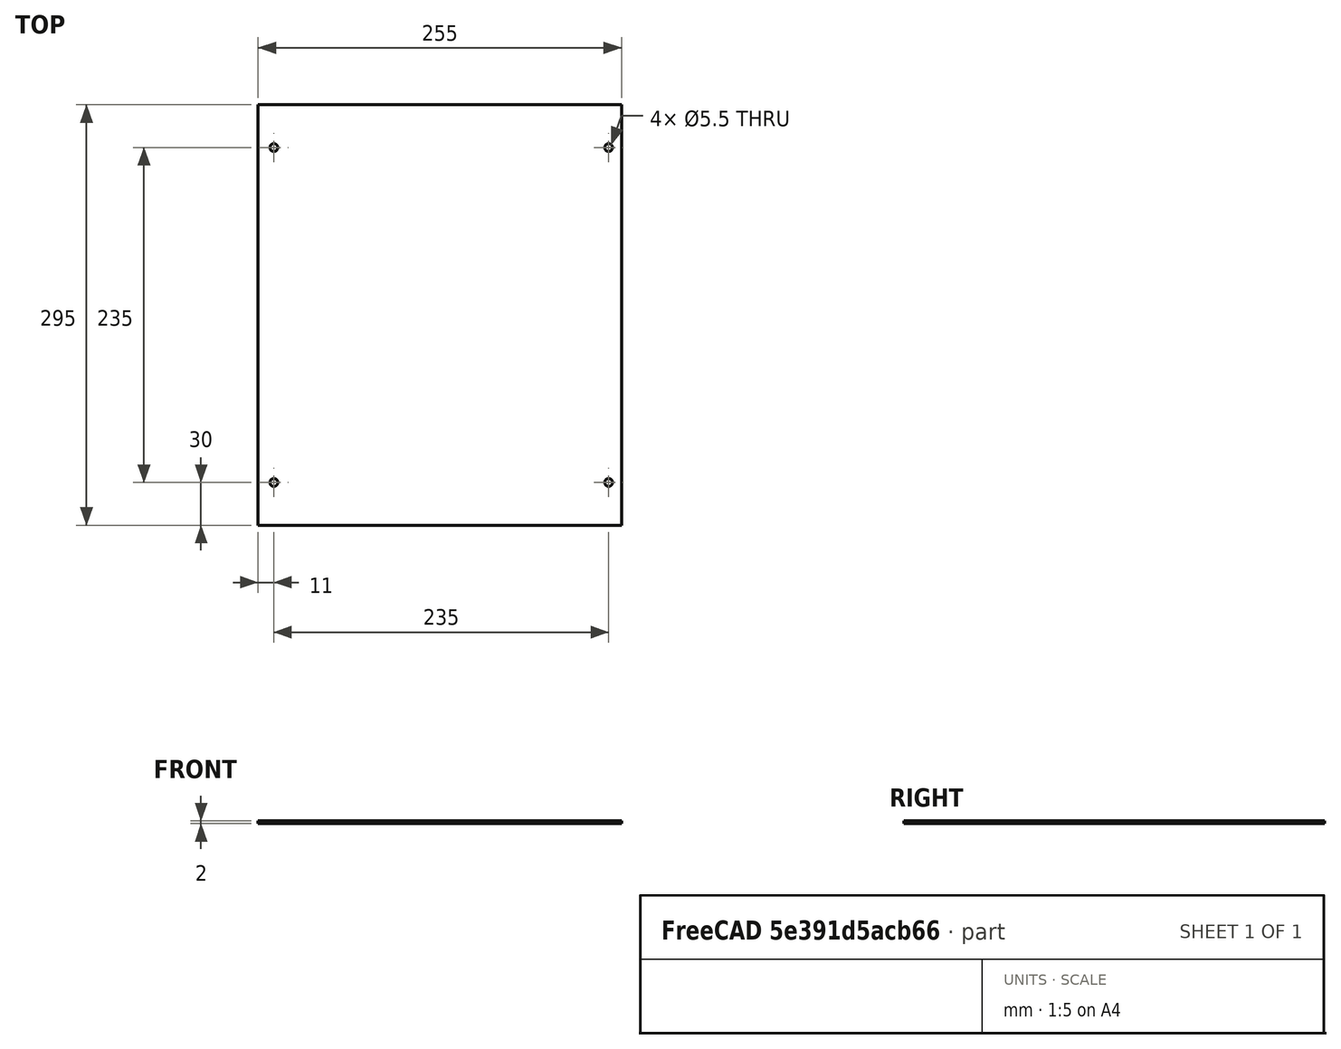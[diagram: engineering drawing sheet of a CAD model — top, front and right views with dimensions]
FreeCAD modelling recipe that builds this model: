
FCSTD DOCUMENT  (FreeCAD 0.15R4671 (Git))
Label: bottom2
License: All rights reserved
LicenseURL: http://en.wikipedia.org/wiki/All_rights_reserved
objects: Drawing::FeatureViewPython×5, Part::Cylinder×4, Part::Cut×4, Part::Box×1, Drawing::FeatureViewPart×1, Drawing::FeaturePage×1
note: 9 computed .brp shape members not serialized (recipe doc carries the construction recipe); baked Part::Feature solids carry a one-line shape summary decoded from their .brp

FEATURE [Part::Box] Box  label="Cube"
  Height = 2
  Length = 255
  Placement = pos=(-1,0,1.5332e-08) rot=(0,0,1;0rad)
  Width = 295
FEATURE [Part::Cylinder] Cylinder
  Angle = 360
  Height = 10
  Placement = pos=(10,30,-5) rot=(0,0,1;0rad)
  Radius = 2.75
FEATURE [Part::Cylinder] Cylinder001
  Angle = 360
  Height = 10
  Placement = pos=(10,265,-5) rot=(0,0,1;0rad)
  Radius = 2.75
FEATURE [Part::Cylinder] Cylinder002
  Angle = 360
  Height = 10
  Placement = pos=(245,30,-5) rot=(0,0,1;0rad)
  Radius = 2.75
FEATURE [Part::Cylinder] Cylinder003
  Angle = 360
  Height = 10
  Placement = pos=(245,265,-5) rot=(0,0,1;0rad)
  Radius = 2.75
FEATURE [Part::Cut] Cut
  Base = -> Box
  Tool = -> Cylinder
FEATURE [Part::Cut] Cut001
  Base = -> Cut
  Tool = -> Cylinder001
FEATURE [Part::Cut] Cut002
  Base = -> Cut001
  Tool = -> Cylinder002
FEATURE [Part::Cut] Cut003
  Base = -> Cut002
  Tool = -> Cylinder003
FEATURE [Drawing::FeatureViewPart] Ortho  label="Ortho_0_0"
  Direction = (0,0,1)
  HiddenWidth = 0.15
  LineWidth = 0.35
  Rotation = 0
  Scale = 0.5
  ShowHiddenLines = false
  ShowSmoothLines = false
  Source = -> Cut003
  Tolerance = 0.05
  ViewResult = <g id="Ortho_0_0"\n   transform="rotate(0,46.75,192.25) translate(46.75,192.25) scale(0.5,0.5)"\n  >\n<g   stroke="rgb(0, 0, 0)"\n   stroke-width="0.7"\n   stroke-linecap="butt"\n   stroke-linejoin="miter"\n   fill="none"\n   transform="scale(1,-1)"\n  >\n<path id= "1" d=" M -1 0 L -1 295 " />\n<path id= "2" d=" M -1 0 L 254 0 " />\n<path id= "3" d=" M -1 295 L 254 295 " />\n<path id= "4" d=" M 254 0 L 254 295 " />\n<circle cx ="245" cy ="265" r ="2.75" /><circle cx ="10" cy ="265" r ="2.75" /><circle cx ="245" cy ="30" r ="2.75" /><circle cx ="10" cy ="30" r ="2.75" /></g>\n</g>
  Visible = true
  X = 46.75
  Y = 192.25
FEATURE [Drawing::FeatureViewPython] dim001  # drawing view (typed FeaturePython)
  Rotation = 0
  ViewResult = <g> \n  <line x1="44.250000" y1="192.250000" x2="37.066293" y2="192.250000" style="stroke:rgb(0,0,255);stroke-width:0.50" />\n<line x1="44.250000" y1="44.750000" x2="37.066293" y2="44.750000" style="stroke:rgb(0,0,255);stroke-width:0.50" />\n<line x1="38.066293" y1="192.250000" x2="38.066293" y2="44.750000" style="stroke:rgb(0,0,255);stroke-width:0.50" /> \n  <polygon points="38.066293,44.750000 37.066293,47.750000 38.066293,48.750000 39.066293,47.750000" style="fill:rgb(0,0,255);stroke:rgb(0,0,255);stroke-width:0" /><polygon points="38.066293,192.250000 39.066293,189.250000 38.066293,188.250000 37.066293,189.250000" style="fill:rgb(0,0,255);stroke:rgb(0,0,255);stroke-width:0" /> \n  <text x="36.066293" y="118.500000" font-family="inherit" font-size="3.6" fill="rgb(0,0,255)" text-anchor="middle" transform="rotate(-90.000000 36.066293,118.500000)" >295</text> </g>
  Visible = true
  X = 0
  Y = 0
  arrowL1 = 3
  arrowL2 = 1
  arrowW = 2
  arrow_scheme = 0
  autoPlaceOffset = 2
  autoPlaceText = true
  click1_x = 38.0663
  click1_y = 84.7282
  click2_x = 38.0663
  click2_y = 84.7282
  comma_decimal_place = false
  dimension_line_overshoot = 1
  gap_datum_points = 2
  halfDimension_linear = false
  lineColor = rgb(0,0,255)
  strokeWidth = 0.5
  textFormat_linear = %(value)3.3f
  textRenderer_color = rgb(0,0,255)
  textRenderer_family = inherit
  textRenderer_size = 3.6
  unit_custom_scale = 1
  unit_scheme = 0
FEATURE [Drawing::FeatureViewPython] dim002  # drawing view (typed FeaturePython)
  Rotation = 0
  ViewResult = <g> \n  <line x1="46.250000" y1="42.750000" x2="46.250000" y2="32.154514" style="stroke:rgb(0,0,255);stroke-width:0.50" />\n<line x1="173.750000" y1="42.750000" x2="173.750000" y2="32.154514" style="stroke:rgb(0,0,255);stroke-width:0.50" />\n<line x1="46.250000" y1="33.154514" x2="173.750000" y2="33.154514" style="stroke:rgb(0,0,255);stroke-width:0.50" /> \n  <polygon points="173.750000,33.154514 170.750000,32.154514 169.750000,33.154514 170.750000,34.154514" style="fill:rgb(0,0,255);stroke:rgb(0,0,255);stroke-width:0" /><polygon points="46.250000,33.154514 49.250000,34.154514 50.250000,33.154514 49.250000,32.154514" style="fill:rgb(0,0,255);stroke:rgb(0,0,255);stroke-width:0" /> \n  <text x="110.000000" y="31.154514" font-family="inherit" font-size="3.6" fill="rgb(0,0,255)" text-anchor="middle" transform="rotate(0.000000 110.000000,31.154514)" >255</text> </g>
  Visible = true
  X = 0
  Y = 0
  arrowL1 = 3
  arrowL2 = 1
  arrowW = 2
  arrow_scheme = 0
  autoPlaceOffset = 2
  autoPlaceText = true
  click1_x = 111.334
  click1_y = 33.1545
  click2_x = 111.334
  click2_y = 33.1545
  comma_decimal_place = false
  dimension_line_overshoot = 1
  gap_datum_points = 2
  halfDimension_linear = false
  lineColor = rgb(0,0,255)
  strokeWidth = 0.5
  textFormat_linear = %(value)3.3f
  textRenderer_color = rgb(0,0,255)
  textRenderer_family = inherit
  textRenderer_size = 3.6
  unit_custom_scale = 1
  unit_scheme = 0
FEATURE [Drawing::FeatureViewPython] dia001  # drawing view (typed FeaturePython)
  Rotation = 0
  ViewResult = <g>  <circle cx ="169.250000" cy ="59.750000" r="0.250000" stroke="none" fill="rgb(0,0,255)" /> \n<line x1="191.968727" y1="59.759988" x2="167.875000" y2="59.749396" style="stroke:rgb(0,0,255);stroke-width:0.50" />\n<polygon points="170.625000,59.750604 173.624560,60.751923 174.624999,59.752363 173.625439,58.751923" style="fill:rgb(0,0,255);stroke:rgb(0,0,255);stroke-width:0" />\n<polygon points="167.875000,59.749396 164.875440,58.748077 163.875001,59.747637 164.874561,60.748077" style="fill:rgb(0,0,255);stroke:rgb(0,0,255);stroke-width:0" />\n<line x1="191.968727" y1="59.759988" x2="179.279963" y2="59.759988" style="stroke:rgb(0,0,255);stroke-width:0.50" />\n<text x="185.624345" y="57.759988" font-family="inherit" font-size="3.6" fill="rgb(0,0,255)" text-anchor="middle" transform="rotate(0.000000 185.624345,57.759988)" >5.5</text> </g>
  Visible = true
  X = 0
  Y = 0
  arrowL1 = 3
  arrowL2 = 1
  arrowW = 2
  arrow_scheme = 0
  autoPlaceOffset = 2
  autoPlaceText = true
  centerPointDia = 0.5
  click1_x = 191.969
  click1_y = 59.76
  click2_x = 179.28
  click2_y = 60.9879
  click3_x = 179.28
  click3_y = 60.9879
  comma_decimal_place = false
  lineColor = rgb(0,0,255)
  strokeWidth = 0.5
  textFormat_circular = 5.5
  textRenderer_color = rgb(0,0,255)
  textRenderer_family = inherit
  textRenderer_size = 3.6
  unit_custom_scale = 1.1
  unit_scheme = 4
FEATURE [Drawing::FeatureViewPython] dimStack001  # drawing view (typed FeaturePython)
  Rotation = 0
  ViewResult = <g> <line x1="169.250000" y1="180.625001" x2="169.250000" y2="213.981497" style="stroke:rgb(0,0,255);stroke-width:0.50" />\n<line x1="173.750000" y1="194.250001" x2="173.750000" y2="213.981497" style="stroke:rgb(0,0,255);stroke-width:0.50" />\n<line x1="169.250000" y1="212.981497" x2="173.750000" y2="212.981497" style="stroke:rgb(0,0,255);stroke-width:0.50" />\n<polygon points="169.250000,212.981497 166.250000,211.981497 165.250000,212.981497 166.250000,213.981497" style="fill:rgb(0,0,255);stroke:rgb(0,0,255);stroke-width:0" />\n<polygon points="173.750000,212.981497 176.750000,213.981497 177.750000,212.981497 176.750000,211.981497" style="fill:rgb(0,0,255);stroke:rgb(0,0,255);stroke-width:0" />\n<text x="171.500000" y="210.981497" font-family="inherit" font-size="3.6" fill="rgb(0,0,255)" text-anchor="middle" transform="rotate(0.000000 171.500000,210.981497)" >10</text> </g> 
  Visible = true
  X = 0
  Y = 0
  arrowL1 = 3
  arrowL2 = 1
  arrowW = 2
  arrow_scheme = 0
  autoPlaceOffset = 2
  click1_x = 175.99
  click1_y = 212.981
  comma_decimal_place = false
  dimension_line_overshoot = 1
  gap_datum_points = 2
  lineColor = rgb(0,0,255)
  stack_offset = -1
  stack_offset0 = 0
  strokeWidth = 0.5
  textFormat_linear = 10
  textRenderer_color = rgb(0,0,255)
  textRenderer_family = inherit
  textRenderer_size = 3.6
  unit_custom_scale = 1.1
  unit_scheme = 4
FEATURE [Drawing::FeatureViewPython] dimStack002  # drawing view (typed FeaturePython)
  Rotation = 0
  ViewResult = <g> <line x1="171.250001" y1="178.625000" x2="191.740782" y2="178.625000" style="stroke:rgb(0,0,255);stroke-width:0.50" />\n<line x1="175.750001" y1="192.250000" x2="191.740782" y2="192.250000" style="stroke:rgb(0,0,255);stroke-width:0.50" />\n<line x1="190.740782" y1="178.625000" x2="190.740782" y2="192.250000" style="stroke:rgb(0,0,255);stroke-width:0.50" />\n<polygon points="190.740782,178.625000 189.740782,181.625000 190.740782,182.625000 191.740782,181.625000" style="fill:rgb(0,0,255);stroke:rgb(0,0,255);stroke-width:0" />\n<polygon points="190.740782,192.250000 191.740782,189.250000 190.740782,188.250000 189.740782,189.250000" style="fill:rgb(0,0,255);stroke:rgb(0,0,255);stroke-width:0" />\n<text x="188.740782" y="185.437500" font-family="inherit" font-size="3.6" fill="rgb(0,0,255)" text-anchor="middle" transform="rotate(-90.000000 188.740782,185.437500)" >30</text> </g> 
  Visible = true
  X = 0
  Y = 0
  arrowL1 = 3
  arrowL2 = 1
  arrowW = 2
  arrow_scheme = 0
  autoPlaceOffset = 2
  click1_x = 190.741
  click1_y = 181.736
  comma_decimal_place = false
  dimension_line_overshoot = 1
  gap_datum_points = 2
  lineColor = rgb(0,0,255)
  stack_offset = 7
  stack_offset0 = 0
  strokeWidth = 0.5
  textFormat_linear = 30
  textRenderer_color = rgb(0,0,255)
  textRenderer_family = inherit
  textRenderer_size = 3.6
  unit_custom_scale = 1.1
  unit_scheme = 4
FEATURE [Drawing::FeaturePage] Page
  EditableTexts = Fichou Dimitri | OCLab bottom | Aluminium - 2 mm thick | Professur für Lebensmittelwissenschaften | Prof. Dr. Gertrud Morlock | A4 | X / Y | SCALE | PART NUMBER | DRAWING NUMBER | YYYY-MM-DD | A
  Group = -> [Ortho,dim001,dim002,dia001,dimStack001,dimStack002]
  Template = <path>
note: 1 file-system path scrubbed to <path> (originals preserved in the JSON sidecar)
